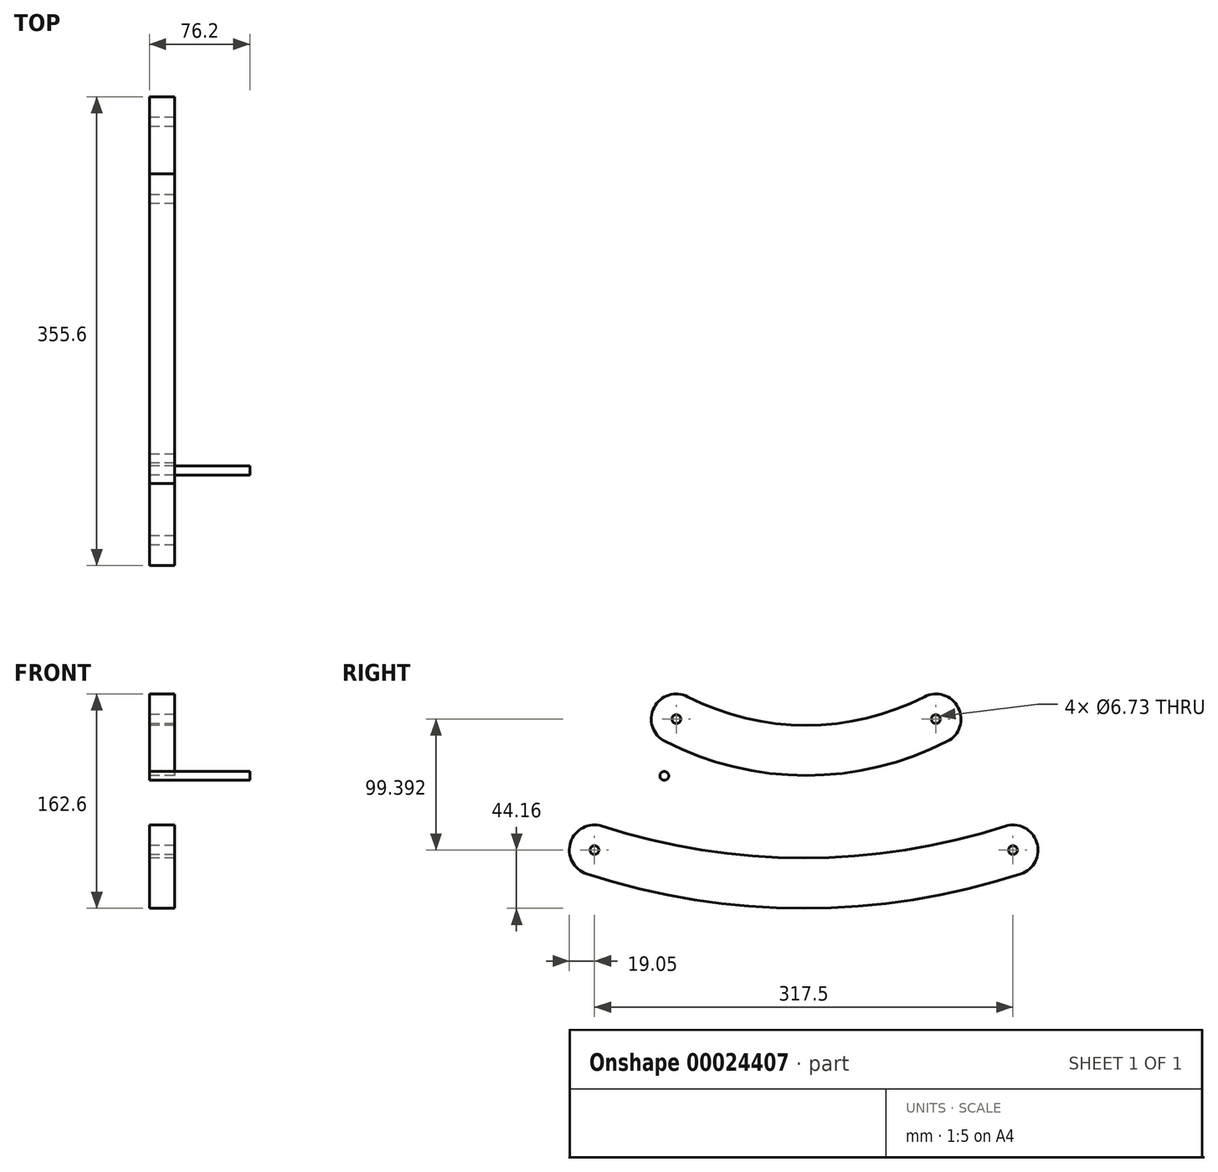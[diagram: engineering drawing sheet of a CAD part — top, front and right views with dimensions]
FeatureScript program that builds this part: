
annotation { "Feature Type Name" : "Feature", "Feature Type Description" : "" }
export const myFeature = defineFeature(function(context is Context, id is Id, definition is map)
    precondition{}
    {
        {
            var Q0;
            Q0=qCreatedBy(makeId("Right.planeOp"),FACE);
            var sketch = newSketch(context, id + "F0", { "sketchPlane" : qUnion([Q0])});
            skCircle(sketch, "E0", {"center": v(0, 0) * mm, "radius": 3.37 * mm});
            skCircle(sketch, "E1", {"center": v(317.5, 0) * mm, "radius": 3.37 * mm});
            skArc(sketch, "E2", {"start": v(5.88, 18.12) * mm, "mid": v(158.75, -6.06) * mm, "end": v(311.62, 18.12) * mm});
            skArc(sketch, "E3", {"start": v(5.88, 18.12) * mm, "mid": v(-18.12, 5.88) * mm, "end": v(-5.88, -18.12) * mm});
            skArc(sketch, "E4", {"start": v(323.38, -18.12) * mm, "mid": v(335.62, 5.88) * mm, "end": v(311.62, 18.12) * mm});
            skArc(sketch, "E5", {"start": v(-5.88, -18.12) * mm, "mid": v(158.75, -44.16) * mm, "end": v(323.38, -18.12) * mm});
            skSolve(sketch);
        }
        {
            var Q0;
            Q0=makeQuery(id+"F0.imprint","IMPRINT",FACE,{"disambiguationData":[TD([[makeQuery(id+"F0.imprint","IMPRINT",EDGE,{"derivedFrom":sQuery(id+"F0.wireOp",EDGE,"E0")}),-1.0]])]});
            extrude(context, id + "F1", {"entities" : qUnion([Q0]), "depth" : 19.05 * mm});
        }
        {
            var Q0;
            Q0=qCreatedBy(makeId("Right.planeOp"),FACE);
            var sketch = newSketch(context, id + "F2", { "sketchPlane" : qUnion([Q0])});
            skCircle(sketch, "E6", {"center": v(52.97, 56.3) * mm, "radius": 3.37 * mm});
            skSolve(sketch);
        }
        {
            var Q0;
            Q0=makeQuery(id+"F2.imprint","IMPRINT",FACE,{"disambiguationData":[TD([[makeQuery(id+"F2.imprint","IMPRINT",EDGE,{"derivedFrom":sQuery(id+"F2.wireOp",EDGE,"E6")}),1.0]])]});
            extrude(context, id + "F3", {"entities" : qUnion([Q0]), "depth" : 76.2 * mm});
        }
        {
            var Q0;
            Q0=qCreatedBy(makeId("Right.planeOp"),FACE);
            var sketch = newSketch(context, id + "F4", { "sketchPlane" : qUnion([Q0])});
            skCircle(sketch, "E7", {"center": v(62.16, 99.4) * mm, "radius": 3.37 * mm});
            skCircle(sketch, "E8", {"center": v(259.01, 99.4) * mm, "radius": 3.37 * mm});
            skArc(sketch, "E9", {"start": v(70.85, 116.35) * mm, "mid": v(45.2, 108.08) * mm, "end": v(53.48, 82.44) * mm});
            skArc(sketch, "E10", {"start": v(267.7, 82.44) * mm, "mid": v(275.97, 108.08) * mm, "end": v(250.33, 116.35) * mm});
            skLineSegment(sketch, "E11", {"start": v(62.16, 99.4) * mm, "end": v(259.01, 99.4) * mm, "construction": true});
            skLineSegment(sketch, "E12", {"start": v(160.59, 99.4) * mm, "end": v(160.59, 291.55) * mm, "construction": true});
            skArc(sketch, "E13", {"start": v(70.85, 116.35) * mm, "mid": v(160.59, 94.7) * mm, "end": v(250.33, 116.35) * mm});
            skArc(sketch, "E14", {"start": v(53.48, 82.44) * mm, "mid": v(160.59, 56.6) * mm, "end": v(267.7, 82.44) * mm});
            skSolve(sketch);
        }
        {
            var Q0;
            Q0=makeQuery(id+"F4.imprint","IMPRINT",FACE,{"disambiguationData":[TD([[makeQuery(id+"F4.imprint","IMPRINT",EDGE,{"derivedFrom":sQuery(id+"F4.wireOp",EDGE,"E7")}),-1.0]])]});
            extrude(context, id + "F5", {"entities" : qUnion([Q0]), "depth" : 19.05 * mm});
        }
    });
